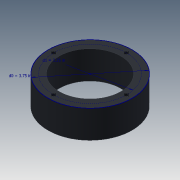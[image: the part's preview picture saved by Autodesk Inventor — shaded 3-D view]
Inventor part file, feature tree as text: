
AUTODESK INVENTOR PART (.ipt)
format: ipt  version: 2020.3 (Build 243373000, 373)  size: 108,032 bytes
history: native  units: in
note: dims shown in document units (in); Inventor stores cm internally (conversion verified against a paired STEP export)
features: sketch x3, extrude x2, hole x2, chamfer x1
ambient origin geometry x8: Origin, YZ Plane, XZ Plane, XY Plane, X Axis, Y Axis, Z Axis, Center Point
bodies: Solid1 (feature_tree)
feature tree (8):
  sketch  "Sketch1"  dims[d0=3.75in d1=3.25in]
  extrude  "Extrusion1"  Depth=3.25in
  hole  "Hole1"  [1 undecoded]
  hole  "Hole2"  [1 undecoded]
  extrude  "Extrusion2"  Depth=0.05in TaperAngle=45.0deg
  chamfer  "Chamfer1"  [1 undecoded]
  sketch  "Sketch2"  dims[d2=1.25in d3=0.0in]
  sketch  "Sketch3"  dims[d4=0.177in d5=0.315in d6=0.375in d7=0.25in d8=0.5635in d9=0.465in d10=0.8108in d11=2.75in d12=0.75in d13=2.5in d14=1.125in d15=0.5635in d16=1.0in d17=0.8108in d18=0.6in d19=1.0in d20=0.0in d21=0.05in d22=0.125in d23=45.0deg]
note: 3 required parameter values undecoded (feature->parameter linkage not recoverable at this tier; creation-order binding heuristic only, values carry confidence <= 0.55)
